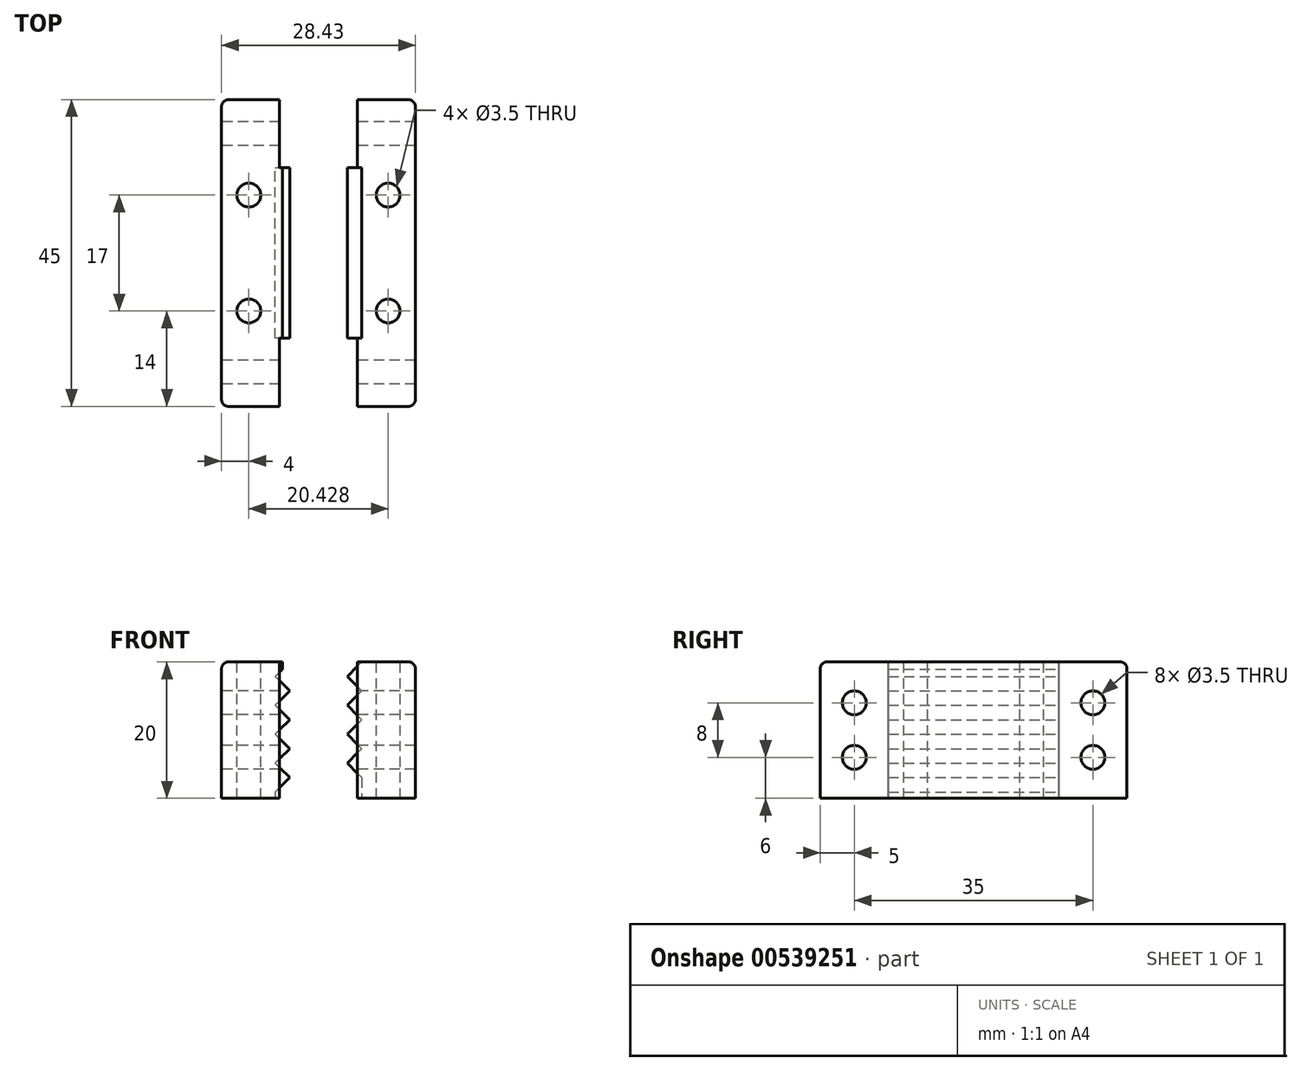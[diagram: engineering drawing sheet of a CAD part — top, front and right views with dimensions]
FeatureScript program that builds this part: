
annotation { "Feature Type Name" : "Feature", "Feature Type Description" : "" }
export const myFeature = defineFeature(function(context is Context, id is Id, definition is map)
    precondition{}
    {
        {
            var Q0;
            Q0=qCreatedBy(makeId("Front.planeOp"),FACE);
            var sketch = newSketch(context, id + "F0", { "sketchPlane" : qUnion([Q0])});
            skLineSegment(sketch, "E0", {"start": v(0, 0) * mm, "end": v(0, 20) * mm});
            skLineSegment(sketch, "E1", {"start": v(0, 20) * mm, "end": v(10, 20) * mm});
            skLineSegment(sketch, "E2", {"start": v(10, 20) * mm, "end": v(10, 0) * mm});
            skLineSegment(sketch, "E3", {"start": v(10, 0) * mm, "end": v(0, 0) * mm});
            skLineSegment(sketch, "E4", {"start": v(10, 20) * mm, "end": v(7.88, 17.88) * mm});
            skLineSegment(sketch, "E5", {"start": v(7.88, 17.88) * mm, "end": v(10, 15.76) * mm});
            skLineSegment(sketch, "E6", {"start": v(10, 15.76) * mm, "end": v(7.88, 13.64) * mm});
            skLineSegment(sketch, "E7", {"start": v(7.88, 13.64) * mm, "end": v(10, 11.51) * mm});
            skLineSegment(sketch, "E8", {"start": v(10, 11.51) * mm, "end": v(7.88, 9.4) * mm});
            skLineSegment(sketch, "E9", {"start": v(7.88, 9.4) * mm, "end": v(10, 7.27) * mm});
            skLineSegment(sketch, "E10", {"start": v(10, 7.27) * mm, "end": v(7.88, 5.15) * mm});
            skLineSegment(sketch, "E11", {"start": v(7.88, 5.15) * mm, "end": v(10, 3.03) * mm});
            skLineSegment(sketch, "E12", {"start": v(10, 3.03) * mm, "end": v(7.88, 0.9) * mm});
            skLineSegment(sketch, "E13", {"start": v(7.88, 0.9) * mm, "end": v(7.88, 0) * mm});
            skLineSegment(sketch, "E14", {"start": v(18.43, 0) * mm, "end": v(28.43, 0) * mm});
            skLineSegment(sketch, "E15", {"start": v(28.43, 0) * mm, "end": v(28.43, 20) * mm});
            skLineSegment(sketch, "E16", {"start": v(28.43, 20) * mm, "end": v(18.43, 20) * mm});
            skLineSegment(sketch, "E17", {"start": v(20.55, 20) * mm, "end": v(18.43, 17.88) * mm});
            skLineSegment(sketch, "E18", {"start": v(18.43, 17.88) * mm, "end": v(20.55, 15.76) * mm});
            skLineSegment(sketch, "E19", {"start": v(20.55, 15.76) * mm, "end": v(18.43, 13.64) * mm});
            skLineSegment(sketch, "E20", {"start": v(18.43, 13.64) * mm, "end": v(20.55, 11.51) * mm});
            skLineSegment(sketch, "E21", {"start": v(20.55, 11.51) * mm, "end": v(18.43, 9.4) * mm});
            skLineSegment(sketch, "E22", {"start": v(18.43, 9.4) * mm, "end": v(20.55, 7.27) * mm});
            skLineSegment(sketch, "E23", {"start": v(20.55, 7.27) * mm, "end": v(18.43, 5.15) * mm});
            skLineSegment(sketch, "E24", {"start": v(18.43, 5.15) * mm, "end": v(20.55, 3.03) * mm});
            skLineSegment(sketch, "E25", {"start": v(20.55, 3.03) * mm, "end": v(18.43, 0.9) * mm});
            skLineSegment(sketch, "E26", {"start": v(18.43, 0.9) * mm, "end": v(18.43, 0) * mm});
            skLineSegment(sketch, "E27", {"start": v(20.55, 3.03) * mm, "end": v(20.55, 0) * mm});
            skLineSegment(sketch, "E28", {"start": v(8.94, 18.94) * mm, "end": v(8.94, 20) * mm});
            skSolve(sketch);
        }
        {
            var Q0;
            {var subQ0=sQuery(id+"F0.wireOp",EDGE,"E0");Q0=makeQuery(id+"F0.imprint","IMPRINT",FACE,{"disambiguationData":[TD([[makeQuery(id+"F0.imprint","IMPRINT",EDGE,{"derivedFrom":subQ0}),-1.0]])]});}
            var Q1;
            {var subQ0=sQuery(id+"F0.wireOp",EDGE,"E15");Q1=makeQuery(id+"F0.imprint","IMPRINT",FACE,{"disambiguationData":[TD([[makeQuery(id+"F0.imprint","IMPRINT",EDGE,{"derivedFrom":subQ0}),1.0]])]});}
            extrude(context, id + "F1", {"entities" : qUnion([Q0, Q1]), "depth" : 25 * mm, "offsetDistance" : 25 * mm});
        }
        {
            var Q0;
            Q0=makeQuery(id+"F1.opExtrude","CAP_FACE",FACE,{"disambiguationData":[OSD([sQuery(id+"F0.wireOp",EDGE,"E14"),sQuery(id+"F0.wireOp",EDGE,"E15"),sQuery(id+"F0.wireOp",EDGE,"E16"),sQuery(id+"F0.wireOp",EDGE,"E17"),sQuery(id+"F0.wireOp",EDGE,"E18"),sQuery(id+"F0.wireOp",EDGE,"E19"),sQuery(id+"F0.wireOp",EDGE,"E20"),sQuery(id+"F0.wireOp",EDGE,"E21"),sQuery(id+"F0.wireOp",EDGE,"E22"),sQuery(id+"F0.wireOp",EDGE,"E23"),sQuery(id+"F0.wireOp",EDGE,"E24"),sQuery(id+"F0.wireOp",EDGE,"E25"),sQuery(id+"F0.wireOp",EDGE,"E26")])],"isStart":false});
            var sketch = newSketch(context, id + "F2", { "sketchPlane" : qUnion([Q0])});
            skLineSegment(sketch, "E29.bottom", {"start": v(28.43, 0) * mm, "end": v(19.93, 0) * mm});
            skLineSegment(sketch, "E29.top", {"start": v(28.43, 20) * mm, "end": v(19.93, 20) * mm});
            skLineSegment(sketch, "E29.left", {"start": v(28.43, 0) * mm, "end": v(28.43, 20) * mm});
            skLineSegment(sketch, "E29.right", {"start": v(19.93, 0) * mm, "end": v(19.93, 20) * mm});
            skLineSegment(sketch, "E30.bottom", {"start": v(0, 0) * mm, "end": v(8.5, 0) * mm});
            skLineSegment(sketch, "E30.top", {"start": v(0, 20) * mm, "end": v(8.5, 20) * mm});
            skLineSegment(sketch, "E30.left", {"start": v(0, 0) * mm, "end": v(0, 20) * mm});
            skLineSegment(sketch, "E30.right", {"start": v(8.5, 0) * mm, "end": v(8.5, 20) * mm});
            skSolve(sketch);
        }
        {
            var Q0;
            Q0 = qSketchRegion(id + "F2", true);
            extrude(context, id + "F3", {"entities" : qUnion([Q0]), "depth" : 10 * mm, "offsetDistance" : 25 * mm});
        }
        {
            var Q0;
            Q0=makeQuery(id+"F1.opExtrude","CAP_FACE",FACE,{"disambiguationData":[OSD([sQuery(id+"F0.wireOp",EDGE,"E14"),sQuery(id+"F0.wireOp",EDGE,"E15"),sQuery(id+"F0.wireOp",EDGE,"E16"),sQuery(id+"F0.wireOp",EDGE,"E17"),sQuery(id+"F0.wireOp",EDGE,"E18"),sQuery(id+"F0.wireOp",EDGE,"E19"),sQuery(id+"F0.wireOp",EDGE,"E20"),sQuery(id+"F0.wireOp",EDGE,"E21"),sQuery(id+"F0.wireOp",EDGE,"E22"),sQuery(id+"F0.wireOp",EDGE,"E23"),sQuery(id+"F0.wireOp",EDGE,"E24"),sQuery(id+"F0.wireOp",EDGE,"E25"),sQuery(id+"F0.wireOp",EDGE,"E26")])],"isStart":true});
            var sketch = newSketch(context, id + "F4", { "sketchPlane" : qUnion([Q0])});
            skLineSegment(sketch, "E31.bottom", {"start": v(-28.43, 0) * mm, "end": v(-19.93, 0) * mm});
            skLineSegment(sketch, "E31.top", {"start": v(-28.43, 20) * mm, "end": v(-19.93, 20) * mm});
            skLineSegment(sketch, "E31.left", {"start": v(-28.43, 0) * mm, "end": v(-28.43, 20) * mm});
            skLineSegment(sketch, "E31.right", {"start": v(-19.93, 0) * mm, "end": v(-19.93, 20) * mm});
            skLineSegment(sketch, "E32.bottom", {"start": v(0, 0) * mm, "end": v(-8.5, 0) * mm});
            skLineSegment(sketch, "E32.top", {"start": v(0, 20) * mm, "end": v(-8.5, 20) * mm});
            skLineSegment(sketch, "E32.left", {"start": v(0, 0) * mm, "end": v(0, 20) * mm});
            skLineSegment(sketch, "E32.right", {"start": v(-8.5, 0) * mm, "end": v(-8.5, 20) * mm});
            skSolve(sketch);
        }
        {
            var Q0;
            Q0 = qSketchRegion(id + "F4", true);
            extrude(context, id + "F5", {"entities" : qUnion([Q0]), "depth" : 10 * mm, "offsetDistance" : 25 * mm});
        }
        {
            var Q0;
            Q0=makeQuery(id+"F5.opExtrude","SWEPT_FACE",FACE,{"disambiguationData":[OSD([sQuery(id+"F4.wireOp",EDGE,"E32.left")])]});
            var sketch = newSketch(context, id + "F6", { "sketchPlane" : qUnion([Q0])});
            skCircle(sketch, "E33", {"center": v(-5, 14) * mm, "radius": 1.75 * mm});
            skCircle(sketch, "E34", {"center": v(-5, 6) * mm, "radius": 1.75 * mm});
            skSolve(sketch);
        }
        {
            var Q0;
            Q0 = qSketchRegion(id + "F6", true);
            extrude(context, id + "F7", {"entities" : qUnion([Q0]), "operationType" : NewBodyOperationType.REMOVE, "oppositeDirection" : true, "depth" : 35 * mm, "offsetDistance" : 25 * mm});
        }
        {
            var Q0;
            Q0=makeQuery(id+"F3.opExtrude","SWEPT_FACE",FACE,{"disambiguationData":[OSD([sQuery(id+"F2.wireOp",EDGE,"E30.left")])]});
            var sketch = newSketch(context, id + "F8", { "sketchPlane" : qUnion([Q0])});
            skCircle(sketch, "E35", {"center": v(30, 14) * mm, "radius": 1.75 * mm});
            skPoint(sketch, "E35.centerSnap0", {"position": v(30, 20) * mm});
            skCircle(sketch, "E36", {"center": v(30, 6) * mm, "radius": 1.75 * mm});
            skSolve(sketch);
        }
        {
            var Q0;
            Q0 = qSketchRegion(id + "F8", true);
            extrude(context, id + "F9", {"entities" : qUnion([Q0]), "operationType" : NewBodyOperationType.REMOVE, "oppositeDirection" : true, "depth" : 25 * mm, "offsetDistance" : 25 * mm});
        }
        {
            var Q0;
            Q0=makeQuery(id+"F3.opExtrude","SWEPT_FACE",FACE,{"disambiguationData":[OSD([sQuery(id+"F2.wireOp",EDGE,"E29.left")])]});
            var sketch = newSketch(context, id + "F10", { "sketchPlane" : qUnion([Q0])});
            skCircle(sketch, "E37", {"center": v(-30, 14) * mm, "radius": 1.75 * mm});
            skCircle(sketch, "E38", {"center": v(-30, 6) * mm, "radius": 1.75 * mm});
            skCircle(sketch, "E39", {"center": v(5, 14) * mm, "radius": 1.75 * mm});
            skCircle(sketch, "E40", {"center": v(5, 6) * mm, "radius": 1.75 * mm});
            skSolve(sketch);
        }
        {
            var Q0;
            Q0 = qSketchRegion(id + "F10", true);
            extrude(context, id + "F11", {"entities" : qUnion([Q0]), "operationType" : NewBodyOperationType.REMOVE, "oppositeDirection" : true, "depth" : 13.2 * mm, "offsetDistance" : 25 * mm});
        }
        {
            var Q0;
            Q0=makeQuery(id+"F1.opExtrude","SWEPT_FACE",FACE,{"disambiguationData":[OSD([sQuery(id+"F0.wireOp",EDGE,"E1")])]});
            var sketch = newSketch(context, id + "F12", { "sketchPlane" : qUnion([Q0])});
            skCircle(sketch, "E41", {"center": v(4, -4) * mm, "radius": 1.75 * mm});
            skCircle(sketch, "E42", {"center": v(4, -21) * mm, "radius": 1.75 * mm});
            skSolve(sketch);
        }
        {
            var Q0;
            Q0 = qSketchRegion(id + "F12", true);
            extrude(context, id + "F13", {"entities" : qUnion([Q0]), "operationType" : NewBodyOperationType.REMOVE, "oppositeDirection" : true, "depth" : 25 * mm, "offsetDistance" : 25 * mm});
        }
        {
            var Q0;
            Q0=makeQuery(id+"F1.opExtrude","SWEPT_FACE",FACE,{"disambiguationData":[OSD([sQuery(id+"F0.wireOp",EDGE,"E16")])]});
            var sketch = newSketch(context, id + "F14", { "sketchPlane" : qUnion([Q0])});
            skCircle(sketch, "E43", {"center": v(24.43, -4) * mm, "radius": 1.75 * mm});
            skCircle(sketch, "E44", {"center": v(24.43, -21) * mm, "radius": 1.75 * mm});
            skSolve(sketch);
        }
        {
            var Q0;
            Q0 = qSketchRegion(id + "F14", true);
            extrude(context, id + "F15", {"entities" : qUnion([Q0]), "operationType" : NewBodyOperationType.REMOVE, "oppositeDirection" : true, "depth" : 25 * mm, "offsetDistance" : 25 * mm});
        }
        {
            var Q0;
            Q0=makeQuery(id+"F3.opExtrude","SWEPT_BODY",BODY,{"disambiguationData":[OSD([sQuery(id+"F2.wireOp",EDGE,"E30.bottom"),sQuery(id+"F2.wireOp",EDGE,"E30.top"),sQuery(id+"F2.wireOp",EDGE,"E30.left"),sQuery(id+"F2.wireOp",EDGE,"E30.right")])]});
            var Q1;
            Q1=makeQuery(id+"F1.opExtrude","SWEPT_BODY",BODY,{"disambiguationData":[OSD([sQuery(id+"F0.wireOp",EDGE,"E0"),sQuery(id+"F0.wireOp",EDGE,"E1"),sQuery(id+"F0.wireOp",EDGE,"E3"),sQuery(id+"F0.wireOp",EDGE,"E4"),sQuery(id+"F0.wireOp",EDGE,"E5"),sQuery(id+"F0.wireOp",EDGE,"E6"),sQuery(id+"F0.wireOp",EDGE,"E7"),sQuery(id+"F0.wireOp",EDGE,"E8"),sQuery(id+"F0.wireOp",EDGE,"E9"),sQuery(id+"F0.wireOp",EDGE,"E10"),sQuery(id+"F0.wireOp",EDGE,"E11"),sQuery(id+"F0.wireOp",EDGE,"E12"),sQuery(id+"F0.wireOp",EDGE,"E13"),sQuery(id+"F0.wireOp",EDGE,"E28")])]});
            var Q2;
            Q2=makeQuery(id+"F5.opExtrude","SWEPT_BODY",BODY,{"disambiguationData":[OSD([sQuery(id+"F4.wireOp",EDGE,"E32.bottom"),sQuery(id+"F4.wireOp",EDGE,"E32.top"),sQuery(id+"F4.wireOp",EDGE,"E32.left"),sQuery(id+"F4.wireOp",EDGE,"E32.right")])]});
            booleanBodies(context, id + "F16", {"operationType" : BooleanOperationType.UNION, "tools" : qUnion([Q0, Q1, Q2])});
        }
        {
            var Q0;
            Q0=makeQuery(id+"F3.opExtrude","SWEPT_BODY",BODY,{"disambiguationData":[OSD([sQuery(id+"F2.wireOp",EDGE,"E29.bottom"),sQuery(id+"F2.wireOp",EDGE,"E29.top"),sQuery(id+"F2.wireOp",EDGE,"E29.left"),sQuery(id+"F2.wireOp",EDGE,"E29.right")])]});
            var Q1;
            Q1=makeQuery(id+"F1.opExtrude","SWEPT_BODY",BODY,{"disambiguationData":[OSD([sQuery(id+"F0.wireOp",EDGE,"E14"),sQuery(id+"F0.wireOp",EDGE,"E15"),sQuery(id+"F0.wireOp",EDGE,"E16"),sQuery(id+"F0.wireOp",EDGE,"E17"),sQuery(id+"F0.wireOp",EDGE,"E18"),sQuery(id+"F0.wireOp",EDGE,"E19"),sQuery(id+"F0.wireOp",EDGE,"E20"),sQuery(id+"F0.wireOp",EDGE,"E21"),sQuery(id+"F0.wireOp",EDGE,"E22"),sQuery(id+"F0.wireOp",EDGE,"E23"),sQuery(id+"F0.wireOp",EDGE,"E24"),sQuery(id+"F0.wireOp",EDGE,"E27")])]});
            var Q2;
            Q2=makeQuery(id+"F5.opExtrude","SWEPT_BODY",BODY,{"disambiguationData":[OSD([sQuery(id+"F4.wireOp",EDGE,"E31.bottom"),sQuery(id+"F4.wireOp",EDGE,"E31.top"),sQuery(id+"F4.wireOp",EDGE,"E31.left"),sQuery(id+"F4.wireOp",EDGE,"E31.right")])]});
            booleanBodies(context, id + "F17", {"operationType" : BooleanOperationType.UNION, "tools" : qUnion([Q0, Q1, Q2])});
        }
        {
            var Q0;
            Q0=makeQuery(id+"F16.opBoolean","MERGE",EDGE,{"derivedFrom":[makeQuery(id+"F1.opExtrude","SWEPT_EDGE",EDGE,{"disambiguationData":[OSD([sQuery(id+"F0.wireOp",EDGE,"E0"),sQuery(id+"F0.wireOp",EDGE,"E1")])]}),makeQuery(id+"F3.opExtrude","SWEPT_EDGE",EDGE,{"disambiguationData":[OSD([sQuery(id+"F2.wireOp",EDGE,"E30.top"),sQuery(id+"F2.wireOp",EDGE,"E30.left")])]}),makeQuery(id+"F5.opExtrude","SWEPT_EDGE",EDGE,{"disambiguationData":[OSD([sQuery(id+"F4.wireOp",EDGE,"E32.top"),sQuery(id+"F4.wireOp",EDGE,"E32.left")])]})]});
            var Q1;
            Q1=makeQuery(id+"F17.opBoolean","MERGE",EDGE,{"derivedFrom":[makeQuery(id+"F1.opExtrude","SWEPT_EDGE",EDGE,{"disambiguationData":[OSD([sQuery(id+"F0.wireOp",EDGE,"E15"),sQuery(id+"F0.wireOp",EDGE,"E16")])]}),makeQuery(id+"F3.opExtrude","SWEPT_EDGE",EDGE,{"disambiguationData":[OSD([sQuery(id+"F2.wireOp",EDGE,"E29.top"),sQuery(id+"F2.wireOp",EDGE,"E29.left")])]}),makeQuery(id+"F5.opExtrude","SWEPT_EDGE",EDGE,{"disambiguationData":[OSD([sQuery(id+"F4.wireOp",EDGE,"E31.top"),sQuery(id+"F4.wireOp",EDGE,"E31.left")])]})]});
            var Q2;
            Q2=makeQuery(id+"F3.opExtrude","CAP_EDGE",EDGE,{"disambiguationData":[OSD([sQuery(id+"F2.wireOp",EDGE,"E29.top")])],"isStart":false});
            var Q3;
            Q3=makeQuery(id+"F5.opExtrude","CAP_EDGE",EDGE,{"disambiguationData":[OSD([sQuery(id+"F4.wireOp",EDGE,"E31.top")])],"isStart":false});
            var Q4;
            Q4=makeQuery(id+"F5.opExtrude","CAP_EDGE",EDGE,{"disambiguationData":[OSD([sQuery(id+"F4.wireOp",EDGE,"E32.top")])],"isStart":false});
            var Q5;
            Q5=makeQuery(id+"F3.opExtrude","CAP_EDGE",EDGE,{"disambiguationData":[OSD([sQuery(id+"F2.wireOp",EDGE,"E30.top")])],"isStart":false});
            var Q6;
            Q6=makeQuery(id+"F5.opExtrude","CAP_EDGE",EDGE,{"disambiguationData":[OSD([sQuery(id+"F4.wireOp",EDGE,"E32.left")])],"isStart":false});
            var Q7;
            Q7=makeQuery(id+"F5.opExtrude","CAP_EDGE",EDGE,{"disambiguationData":[OSD([sQuery(id+"F4.wireOp",EDGE,"E31.left")])],"isStart":false});
            var Q8;
            Q8=makeQuery(id+"F3.opExtrude","CAP_EDGE",EDGE,{"disambiguationData":[OSD([sQuery(id+"F2.wireOp",EDGE,"E30.left")])],"isStart":false});
            var Q9;
            Q9=makeQuery(id+"F3.opExtrude","CAP_EDGE",EDGE,{"disambiguationData":[OSD([sQuery(id+"F2.wireOp",EDGE,"E29.left")])],"isStart":false});
            fillet(context, id + "F18", {"entities" : qUnion([Q0, Q1, Q2, Q3, Q4, Q5, Q6, Q7, Q8, Q9]), "radius" : 1 * mm, "tangentPropagation" : true, "allowEdgeOverflow" : false});
        }
    });
